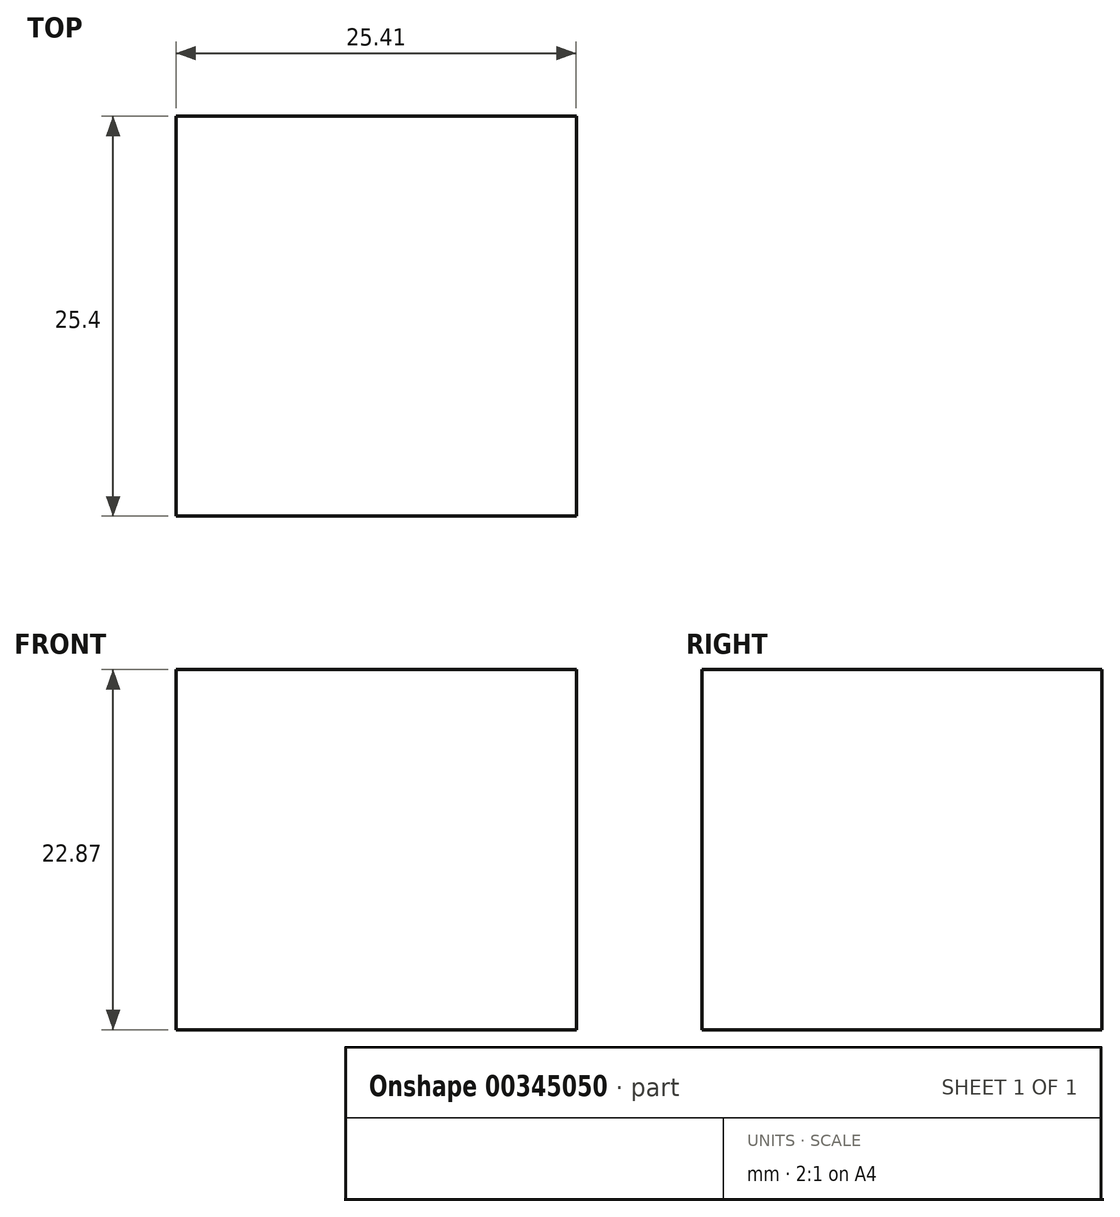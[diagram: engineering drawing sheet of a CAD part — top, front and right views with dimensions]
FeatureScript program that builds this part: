
annotation { "Feature Type Name" : "Feature", "Feature Type Description" : "" }
export const myFeature = defineFeature(function(context is Context, id is Id, definition is map)
    precondition{}
    {
        {
            var Q0;
            Q0=qCreatedBy(makeId("Front.planeOp"),FACE);
            var sketch = newSketch(context, id + "F0", { "sketchPlane" : qUnion([Q0])});
            skLineSegment(sketch, "E0.bottom", {"start": v(-64.36, 52.54) * mm, "end": v(-38.95, 52.54) * mm});
            skLineSegment(sketch, "E0.top", {"start": v(-64.36, 29.67) * mm, "end": v(-38.95, 29.67) * mm});
            skLineSegment(sketch, "E0.left", {"start": v(-64.36, 52.54) * mm, "end": v(-64.36, 29.67) * mm});
            skLineSegment(sketch, "E0.right", {"start": v(-38.95, 52.54) * mm, "end": v(-38.95, 29.67) * mm});
            skLineSegment(sketch, "E1.bottom", {"start": v(-59.09, 46.23) * mm, "end": v(-42.8, 46.23) * mm});
            skLineSegment(sketch, "E1.top", {"start": v(-59.09, 33.88) * mm, "end": v(-42.8, 33.88) * mm});
            skLineSegment(sketch, "E1.left", {"start": v(-59.09, 46.23) * mm, "end": v(-59.09, 33.88) * mm});
            skLineSegment(sketch, "E1.right", {"start": v(-42.8, 46.23) * mm, "end": v(-42.8, 33.88) * mm});
            skSolve(sketch);
        }
        {
            var Q0;
            Q0=makeQuery(id+"F0.imprint","IMPRINT",FACE,{"disambiguationData":[TD([[makeQuery(id+"F0.imprint","IMPRINT",EDGE,{"derivedFrom":sQuery(id+"F0.wireOp",EDGE,"E1.bottom")}),-1.0]])]});
            var Q1;
            Q1=makeQuery(id+"F0.imprint","IMPRINT",FACE,{"disambiguationData":[TD([[makeQuery(id+"F0.imprint","IMPRINT",EDGE,{"derivedFrom":sQuery(id+"F0.wireOp",EDGE,"E0.bottom")}),-1.0]])]});
            extrude(context, id + "F1", {"entities" : qUnion([Q0, Q1]), "depth" : 25.4 * mm});
        }
    });
